# Revit family: CI804ZDTB5-AA-SG-SEA
name_source: partatom
category: Specialty Equipment
units: mm (PartAtom-declared; Revit-internal decimal feet)

## family parameters
Always vertical = No
Cut with Voids When Loaded = Yes
Part Type = Normal
Room Calculation Point = No
Round Connector Dimension = Use Diameter
Shared = No
Work Plane-Based = Yes

## types (1)
- CI804ZDTB5
    Cavity - Depth = 490 mm  [stored 1.60761 ft]
    Cavity - Height = 2260 mm
    Cavity - Width = 720 mm  [stored 2.3622 ft]
    Clearance - Below Cooktop = 86 mm  [stored 0.282152 ft]
    Clearance - Overhead Rangehood = 650 mm  [stored 2.13255 ft]
    Default Elevation = 0 mm  [stored 0 ft]
    Description = 80cm Series 7 Induction cooktop
    Manufacturer = Fisher & Paykel Appliances
    Material - Cooktop = Fisher & Paykel - Glass, Black
    Model = CI804ZDTB5
    Product - Depth = 528 mm  [stored 1.73228 ft]
    Product - Height = 90 mm  [stored 0.295276 ft]
    Product - Width = 798 mm
    URL = www.fisherpaykel.com

note: [stored X ft] marks values corroborated as IEEE doubles in the binary element streams (Revit-internal decimal feet)

## geometry (parser evidence)
native form markers: Sweep x109
no freeform markers — native parametric forms only
